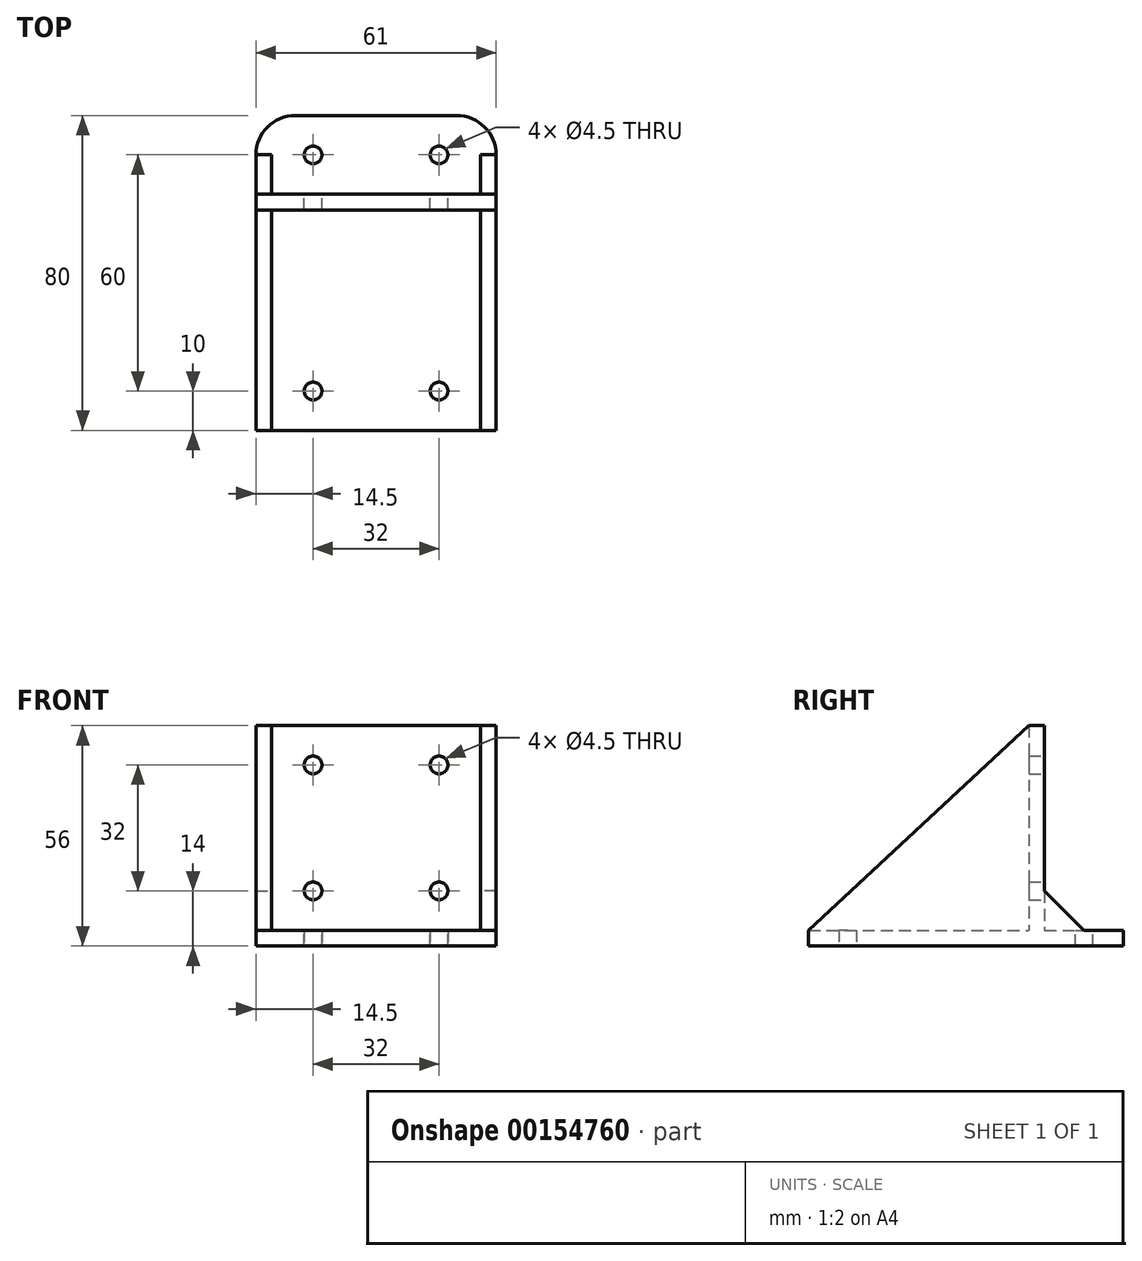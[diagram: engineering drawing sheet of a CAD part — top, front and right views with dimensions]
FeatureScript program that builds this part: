
annotation { "Feature Type Name" : "Feature", "Feature Type Description" : "" }
export const myFeature = defineFeature(function(context is Context, id is Id, definition is map)
    precondition{}
    {
        {
            var Q0;
            Q0=qCreatedBy(makeId("Top.planeOp"),FACE);
            var sketch = newSketch(context, id + "F0", { "sketchPlane" : qUnion([Q0])});
            skLineSegment(sketch, "E0.bottom", {"start": v(26.5, -30) * mm, "end": v(-26.5, -30) * mm});
            skLineSegment(sketch, "E0.top", {"start": v(26.5, 30) * mm, "end": v(-26.5, 30) * mm});
            skLineSegment(sketch, "E0.left", {"start": v(26.5, -30) * mm, "end": v(26.5, 30) * mm});
            skLineSegment(sketch, "E0.right", {"start": v(-26.5, -30) * mm, "end": v(-26.5, 30) * mm});
            skPoint(sketch, "E0.middle", {"position": v(0, 0) * mm});
            skSolve(sketch);
        }
        {
            var Q0;
            Q0=makeQuery(id+"F0.imprint","IMPRINT",FACE,{"disambiguationData":[TD([[makeQuery(id+"F0.imprint","IMPRINT",EDGE,{"derivedFrom":sQuery(id+"F0.wireOp",EDGE,"E0.bottom")}),-1.0]])]});
            extrude(context, id + "F1", {"entities" : qUnion([Q0]), "depth" : 4 * mm});
        }
        {
            var Q0;
            Q0=makeQuery(id+"F1.opExtrude","CAP_FACE",FACE,{"disambiguationData":[OSD([sQuery(id+"F0.wireOp",EDGE,"E0.bottom"),sQuery(id+"F0.wireOp",EDGE,"E0.top"),sQuery(id+"F0.wireOp",EDGE,"E0.left"),sQuery(id+"F0.wireOp",EDGE,"E0.right")])],"isStart":false});
            var sketch = newSketch(context, id + "F2", { "sketchPlane" : qUnion([Q0])});
            skLineSegment(sketch, "E1.bottom", {"start": v(-26.5, 30) * mm, "end": v(26.5, 30) * mm});
            skLineSegment(sketch, "E1.top", {"start": v(-26.5, 26) * mm, "end": v(26.5, 26) * mm});
            skLineSegment(sketch, "E1.left", {"start": v(-26.5, 30) * mm, "end": v(-26.5, 26) * mm});
            skLineSegment(sketch, "E1.right", {"start": v(26.5, 30) * mm, "end": v(26.5, 26) * mm});
            skSolve(sketch);
        }
        {
            var Q0;
            Q0 = qSketchRegion(id + "F2", true);
            extrude(context, id + "F3", {"entities" : qUnion([Q0]), "operationType" : NewBodyOperationType.ADD, "depth" : 52 * mm});
        }
        {
            var Q0;
            Q0=makeQuery(id+"F1.opExtrude","CAP_FACE",FACE,{"disambiguationData":[OSD([sQuery(id+"F0.wireOp",EDGE,"E0.bottom"),sQuery(id+"F0.wireOp",EDGE,"E0.top"),sQuery(id+"F0.wireOp",EDGE,"E0.left"),sQuery(id+"F0.wireOp",EDGE,"E0.right")])],"isStart":true});
            var sketch = newSketch(context, id + "F4", { "sketchPlane" : qUnion([Q0])});
            skCircle(sketch, "E2", {"center": v(-16, 20) * mm, "radius": 2.25 * mm});
            skCircle(sketch, "E3.1.0.0", {"center": v(16, 20) * mm, "radius": 2.25 * mm});
            skLineSegment(sketch, "E3.direction1", {"start": v(-16, 20) * mm, "end": v(16, 20) * mm, "construction": true});
            skLineSegment(sketch, "E3.direction2", {"start": v(-16, 20) * mm, "end": v(-16, -20) * mm, "construction": true});
            skSolve(sketch);
        }
        {
            var Q0;
            Q0=makeQuery(id+"F4.imprint","IMPRINT",FACE,{"disambiguationData":[TD([[makeQuery(id+"F4.imprint","IMPRINT",EDGE,{"derivedFrom":sQuery(id+"F4.wireOp",EDGE,"E2")}),1.0]])]});
            var Q1;
            Q1=makeQuery(id+"F4.imprint","IMPRINT",FACE,{"disambiguationData":[TD([[makeQuery(id+"F4.imprint","IMPRINT",EDGE,{"derivedFrom":sQuery(id+"F4.wireOp",EDGE,"E3.1.0.0")}),1.0]])]});
            var Q2;
            Q2=makeQuery(id+"F4.imprint","IMPRINT",FACE,{"disambiguationData":[TD([[makeQuery(id+"F4.imprint","IMPRINT",EDGE,{"derivedFrom":sQuery(id+"F4.wireOp",EDGE,"E3.1.1.0")}),1.0]])]});
            var Q3;
            Q3=makeQuery(id+"F4.imprint","IMPRINT",FACE,{"disambiguationData":[TD([[makeQuery(id+"F4.imprint","IMPRINT",EDGE,{"derivedFrom":sQuery(id+"F4.wireOp",EDGE,"E3.0.1.0")}),1.0]])]});
            extrude(context, id + "F5", {"entities" : qUnion([Q0, Q1, Q2, Q3]), "operationType" : NewBodyOperationType.REMOVE, "endBound" : BoundingType.THROUGH_ALL, "oppositeDirection" : true, "depth" : 25 * mm});
        }
        {
            var Q0;
            Q0=makeQuery(id+"F3.boolean.opBoolean","MERGE",FACE,{"derivedFrom":[makeQuery(id+"F1.opExtrude","SWEPT_FACE",FACE,{"disambiguationData":[OSD([sQuery(id+"F0.wireOp",EDGE,"E0.top")])]}),makeQuery(id+"F3.opExtrude","SWEPT_FACE",FACE,{"disambiguationData":[OSD([sQuery(id+"F2.wireOp",EDGE,"E1.bottom")])]})]});
            var sketch = newSketch(context, id + "F6", { "sketchPlane" : qUnion([Q0])});
            skCircle(sketch, "E4.0.1.0", {"center": v(-16, 14) * mm, "radius": 2.25 * mm});
            skCircle(sketch, "E5.0.1.0", {"center": v(-16, 46) * mm, "radius": 2.25 * mm});
            skCircle(sketch, "E5.1.0.0", {"center": v(16, 14) * mm, "radius": 2.25 * mm});
            skCircle(sketch, "E5.1.1.0", {"center": v(16, 46) * mm, "radius": 2.25 * mm});
            skLineSegment(sketch, "E5.direction1", {"start": v(-16, 14) * mm, "end": v(16, 14) * mm, "construction": true});
            skLineSegment(sketch, "E5.direction2", {"start": v(-16, 14) * mm, "end": v(-16, 46) * mm, "construction": true});
            skSolve(sketch);
        }
        {
            var Q0;
            Q0 = qSketchRegion(id + "F6", true);
            extrude(context, id + "F7", {"entities" : qUnion([Q0]), "operationType" : NewBodyOperationType.REMOVE, "endBound" : BoundingType.THROUGH_ALL, "oppositeDirection" : true, "depth" : 25 * mm});
        }
        {
            var Q0;
            Q0=makeQuery(id+"F3.boolean.opBoolean","MERGE",FACE,{"derivedFrom":[makeQuery(id+"F1.opExtrude","SWEPT_FACE",FACE,{"disambiguationData":[OSD([sQuery(id+"F0.wireOp",EDGE,"E0.left")])]}),makeQuery(id+"F3.opExtrude","SWEPT_FACE",FACE,{"disambiguationData":[OSD([sQuery(id+"F2.wireOp",EDGE,"E1.right")])]})]});
            var sketch = newSketch(context, id + "F8", { "sketchPlane" : qUnion([Q0])});
            skLineSegment(sketch, "E6", {"start": v(30, 56) * mm, "end": v(30, 0) * mm});
            skLineSegment(sketch, "E7", {"start": v(30, 0) * mm, "end": v(-30, 0) * mm});
            skLineSegment(sketch, "E8", {"start": v(-30, 0) * mm, "end": v(-30, 4) * mm});
            skLineSegment(sketch, "E9", {"start": v(-30, 4) * mm, "end": v(26, 56) * mm});
            skLineSegment(sketch, "E10", {"start": v(26, 56) * mm, "end": v(30, 56) * mm});
            skLineSegment(sketch, "E11", {"start": v(30, 4) * mm, "end": v(40, 4) * mm});
            skLineSegment(sketch, "E12", {"start": v(40, 4) * mm, "end": v(30, 14) * mm});
            skSolve(sketch);
        }
        {
            var Q0;
            Q0 = qSketchRegion(id + "F8", true);
            extrude(context, id + "F9", {"entities" : qUnion([Q0]), "operationType" : NewBodyOperationType.ADD, "depth" : 4 * mm});
        }
        {
            var Q0;
            Q0=makeQuery(id+"F3.boolean.opBoolean","MERGE",FACE,{"derivedFrom":[makeQuery(id+"F1.opExtrude","SWEPT_FACE",FACE,{"disambiguationData":[OSD([sQuery(id+"F0.wireOp",EDGE,"E0.right")])]}),makeQuery(id+"F3.opExtrude","SWEPT_FACE",FACE,{"disambiguationData":[OSD([sQuery(id+"F2.wireOp",EDGE,"E1.left")])]})]});
            var sketch = newSketch(context, id + "F10", { "sketchPlane" : qUnion([Q0])});
            skLineSegment(sketch, "E13", {"start": v(-30, 56) * mm, "end": v(-26, 56) * mm});
            skLineSegment(sketch, "E14", {"start": v(-26, 56) * mm, "end": v(30, 4) * mm});
            skLineSegment(sketch, "E15", {"start": v(30, 4) * mm, "end": v(30, 0) * mm});
            skLineSegment(sketch, "E16", {"start": v(30, 0) * mm, "end": v(-30, 0) * mm});
            skLineSegment(sketch, "E17", {"start": v(-30, 0) * mm, "end": v(-30, 56) * mm});
            skLineSegment(sketch, "E18", {"start": v(-30, 4) * mm, "end": v(-40, 4) * mm});
            skLineSegment(sketch, "E19", {"start": v(-40, 4) * mm, "end": v(-30, 14) * mm});
            skLineSegment(sketch, "E20", {"start": v(-30, 14) * mm, "end": v(-30, 4) * mm});
            skSolve(sketch);
        }
        {
            var Q0;
            Q0 = qSketchRegion(id + "F10", true);
            extrude(context, id + "F11", {"entities" : qUnion([Q0]), "operationType" : NewBodyOperationType.ADD, "depth" : 4 * mm});
        }
        {
            var Q0;
            Q0=makeQuery(id+"F11.boolean.opBoolean","MERGE",FACE,{"derivedFrom":[makeQuery(id+"F9.boolean.opBoolean","MERGE",FACE,{"derivedFrom":[makeQuery(id+"F3.boolean.opBoolean","MERGE",FACE,{"derivedFrom":[makeQuery(id+"F1.opExtrude","SWEPT_FACE",FACE,{"disambiguationData":[OSD([sQuery(id+"F0.wireOp",EDGE,"E0.top")])]}),makeQuery(id+"F3.opExtrude","SWEPT_FACE",FACE,{"disambiguationData":[OSD([sQuery(id+"F2.wireOp",EDGE,"E1.bottom")])]})]}),makeQuery(id+"F9.opExtrude","SWEPT_FACE",FACE,{"disambiguationData":[OSD([sQuery(id+"F8.wireOp",EDGE,"E6")])]})]}),makeQuery(id+"F11.opExtrude","SWEPT_FACE",FACE,{"disambiguationData":[OSD([sQuery(id+"F10.wireOp",EDGE,"E17")])]})]});
            var sketch = newSketch(context, id + "F12", { "sketchPlane" : qUnion([Q0])});
            skLineSegment(sketch, "E21.bottom", {"start": v(-30.5, 0) * mm, "end": v(30.5, 0) * mm});
            skLineSegment(sketch, "E21.top", {"start": v(-30.5, 4) * mm, "end": v(30.5, 4) * mm});
            skLineSegment(sketch, "E21.left", {"start": v(-30.5, 0) * mm, "end": v(-30.5, 4) * mm});
            skLineSegment(sketch, "E21.right", {"start": v(30.5, 0) * mm, "end": v(30.5, 4) * mm});
            skSolve(sketch);
        }
        {
            var Q0;
            Q0 = qSketchRegion(id + "F12", true);
            extrude(context, id + "F13", {"entities" : qUnion([Q0]), "operationType" : NewBodyOperationType.ADD, "depth" : 20 * mm});
        }
        {
            var Q0;
            Q0=makeQuery(id+"F13.opExtrude","SWEPT_FACE",FACE,{"disambiguationData":[OSD([sQuery(id+"F12.wireOp",EDGE,"E21.top")])]});
            var sketch = newSketch(context, id + "F14", { "sketchPlane" : qUnion([Q0])});
            skCircle(sketch, "E22", {"center": v(-16, 40) * mm, "radius": 2.25 * mm});
            skCircle(sketch, "E23", {"center": v(16, 40) * mm, "radius": 2.25 * mm});
            skSolve(sketch);
        }
        {
            var Q0;
            Q0=makeQuery(id+"F14.imprint","IMPRINT",FACE,{"disambiguationData":[TD([[makeQuery(id+"F14.imprint","IMPRINT",EDGE,{"derivedFrom":sQuery(id+"F14.wireOp",EDGE,"E23")}),1.0]])]});
            var Q1;
            Q1=makeQuery(id+"F14.imprint","IMPRINT",FACE,{"disambiguationData":[TD([[makeQuery(id+"F14.imprint","IMPRINT",EDGE,{"derivedFrom":sQuery(id+"F14.wireOp",EDGE,"E22")}),1.0]])]});
            extrude(context, id + "F15", {"entities" : qUnion([Q0, Q1]), "operationType" : NewBodyOperationType.REMOVE, "endBound" : BoundingType.THROUGH_ALL, "oppositeDirection" : true, "depth" : 25 * mm});
        }
        {
            var Q0;
            Q0=makeQuery(id+"F13.opExtrude","CAP_EDGE",EDGE,{"disambiguationData":[OSD([sQuery(id+"F12.wireOp",EDGE,"E21.left")])],"isStart":false});
            var Q1;
            Q1=makeQuery(id+"F13.opExtrude","CAP_EDGE",EDGE,{"disambiguationData":[OSD([sQuery(id+"F12.wireOp",EDGE,"E21.right")])],"isStart":false});
            fillet(context, id + "F16", {"entities" : qUnion([Q0, Q1]), "radius" : 10 * mm, "tangentPropagation" : true, "allowEdgeOverflow" : false});
        }
    });
